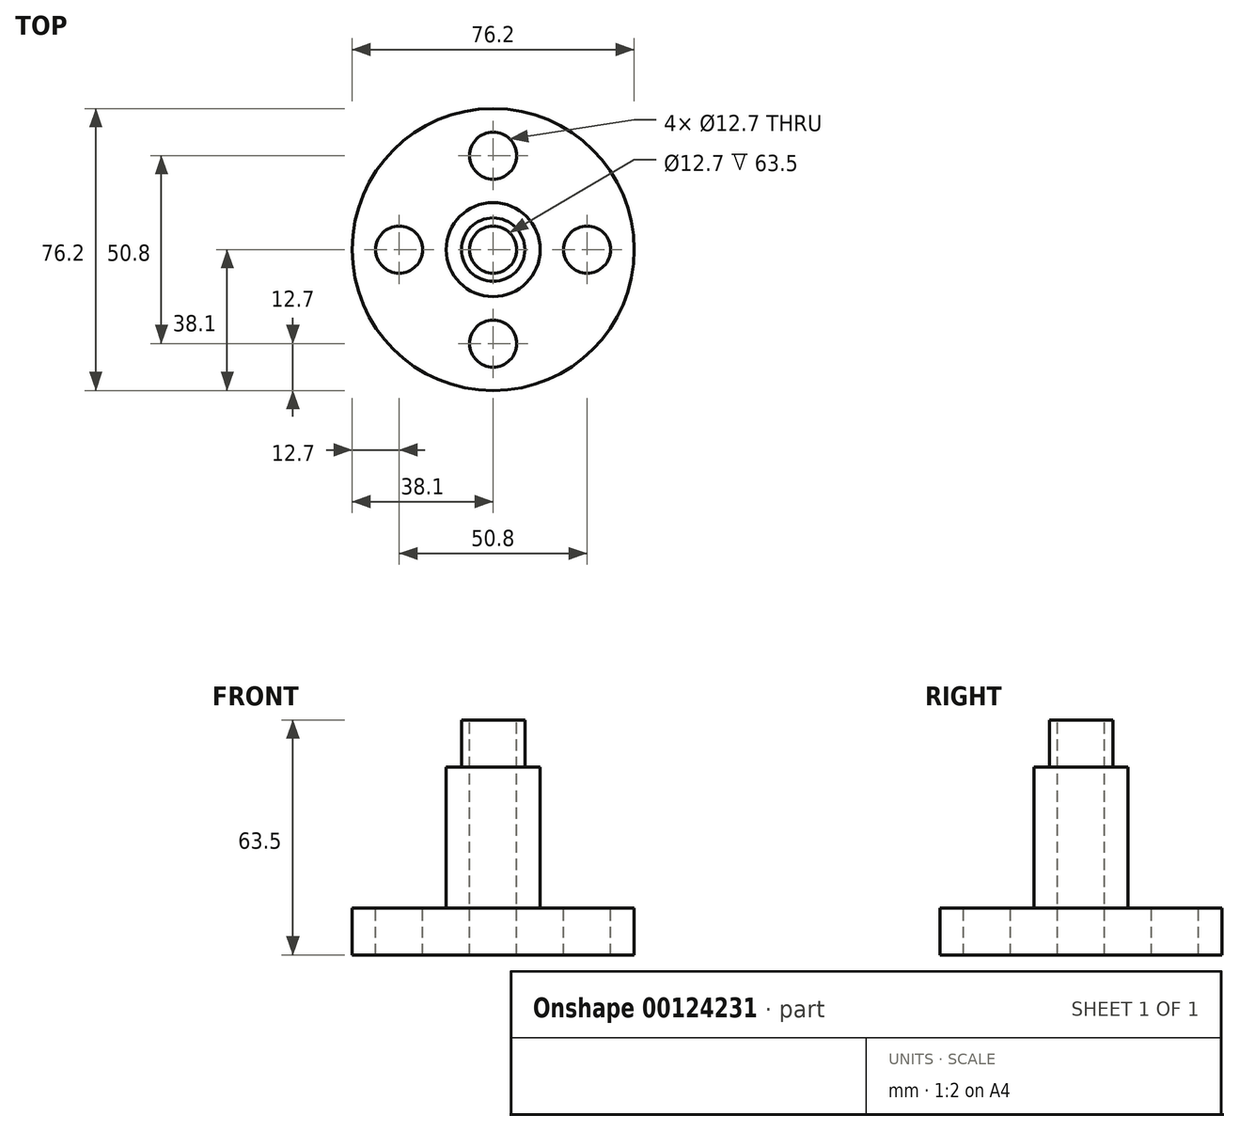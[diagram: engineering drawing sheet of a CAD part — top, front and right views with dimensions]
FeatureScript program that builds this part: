
annotation { "Feature Type Name" : "Feature", "Feature Type Description" : "" }
export const myFeature = defineFeature(function(context is Context, id is Id, definition is map)
    precondition{}
    {
        {
            var Q0;
            Q0=qCreatedBy(makeId("Top.planeOp"),FACE);
            var sketch = newSketch(context, id + "F0", { "sketchPlane" : qUnion([Q0])});
            skCircle(sketch, "E0", {"center": v(0, 0) * mm, "radius": 38.1 * mm});
            skSolve(sketch);
        }
        {
            var Q0;
            Q0 = qSketchRegion(id + "F0", true);
            extrude(context, id + "F1", {"entities" : qUnion([Q0]), "depth" : 12.7 * mm});
        }
        {
            var Q0;
            Q0=makeQuery(id+"F1.opExtrude","CAP_FACE",FACE,{"disambiguationData":[OSD([sQuery(id+"F0.wireOp",EDGE,"E0")])],"isStart":false});
            var sketch = newSketch(context, id + "F2", { "sketchPlane" : qUnion([Q0])});
            skCircle(sketch, "E1", {"center": v(0, 25.4) * mm, "radius": 6.35 * mm});
            skCircle(sketch, "E2", {"center": v(-25.4, 0) * mm, "radius": 6.35 * mm});
            skCircle(sketch, "E3", {"center": v(0, -25.4) * mm, "radius": 6.35 * mm});
            skCircle(sketch, "E4", {"center": v(25.4, 0) * mm, "radius": 6.35 * mm});
            skSolve(sketch);
        }
        {
            var Q0;
            Q0=makeQuery(id+"F2.imprint","IMPRINT",FACE,{"disambiguationData":[TD([[makeQuery(id+"F2.imprint","IMPRINT",EDGE,{"derivedFrom":sQuery(id+"F2.wireOp",EDGE,"E1")}),1.0]])]});
            var Q1;
            Q1=makeQuery(id+"F2.imprint","IMPRINT",FACE,{"disambiguationData":[TD([[makeQuery(id+"F2.imprint","IMPRINT",EDGE,{"derivedFrom":sQuery(id+"F2.wireOp",EDGE,"E4")}),1.0]])]});
            var Q2;
            Q2=makeQuery(id+"F2.imprint","IMPRINT",FACE,{"disambiguationData":[TD([[makeQuery(id+"F2.imprint","IMPRINT",EDGE,{"derivedFrom":sQuery(id+"F2.wireOp",EDGE,"E3")}),1.0]])]});
            var Q3;
            Q3=makeQuery(id+"F2.imprint","IMPRINT",FACE,{"disambiguationData":[TD([[makeQuery(id+"F2.imprint","IMPRINT",EDGE,{"derivedFrom":sQuery(id+"F2.wireOp",EDGE,"E2")}),1.0]])]});
            extrude(context, id + "F3", {"entities" : qUnion([Q0, Q1, Q2, Q3]), "operationType" : NewBodyOperationType.REMOVE, "endBound" : BoundingType.THROUGH_ALL, "oppositeDirection" : true, "depth" : 25.4 * mm});
        }
        {
            var Q0;
            Q0=makeQuery(id+"F1.opExtrude","CAP_FACE",FACE,{"disambiguationData":[OSD([sQuery(id+"F0.wireOp",EDGE,"E0")])],"isStart":false});
            var sketch = newSketch(context, id + "F4", { "sketchPlane" : qUnion([Q0])});
            skCircle(sketch, "E5", {"center": v(0, 0) * mm, "radius": 12.7 * mm});
            skSolve(sketch);
        }
        {
            var Q0;
            Q0=makeQuery(id+"F4.imprint","IMPRINT",FACE,{"disambiguationData":[TD([[makeQuery(id+"F4.imprint","IMPRINT",EDGE,{"derivedFrom":sQuery(id+"F4.wireOp",EDGE,"E5")}),1.0]])]});
            extrude(context, id + "F5", {"entities" : qUnion([Q0]), "operationType" : NewBodyOperationType.ADD, "depth" : 38.1 * mm});
        }
        {
            var Q0;
            Q0=makeQuery(id+"F5.opExtrude","CAP_FACE",FACE,{"disambiguationData":[OSD([sQuery(id+"F4.wireOp",EDGE,"E5")])],"isStart":false});
            var sketch = newSketch(context, id + "F6", { "sketchPlane" : qUnion([Q0])});
            skCircle(sketch, "E6", {"center": v(0, 0) * mm, "radius": 8.57 * mm});
            skSolve(sketch);
        }
        {
            var Q0;
            Q0=makeQuery(id+"F6.imprint","IMPRINT",FACE,{"disambiguationData":[TD([[makeQuery(id+"F6.imprint","IMPRINT",EDGE,{"derivedFrom":sQuery(id+"F6.wireOp",EDGE,"E6")}),1.0]])]});
            extrude(context, id + "F7", {"entities" : qUnion([Q0]), "operationType" : NewBodyOperationType.ADD, "depth" : 12.7 * mm});
        }
        {
            var Q0;
            Q0=makeQuery(id+"F7.opExtrude","CAP_FACE",FACE,{"disambiguationData":[OSD([sQuery(id+"F6.wireOp",EDGE,"E6")])],"isStart":false});
            var sketch = newSketch(context, id + "F8", { "sketchPlane" : qUnion([Q0])});
            skCircle(sketch, "E7", {"center": v(0, 0) * mm, "radius": 6.35 * mm});
            skSolve(sketch);
        }
        {
            var Q0;
            Q0 = qSketchRegion(id + "F8", true);
            extrude(context, id + "F9", {"entities" : qUnion([Q0]), "operationType" : NewBodyOperationType.REMOVE, "endBound" : BoundingType.THROUGH_ALL, "oppositeDirection" : true, "depth" : 25.4 * mm});
        }
    });
